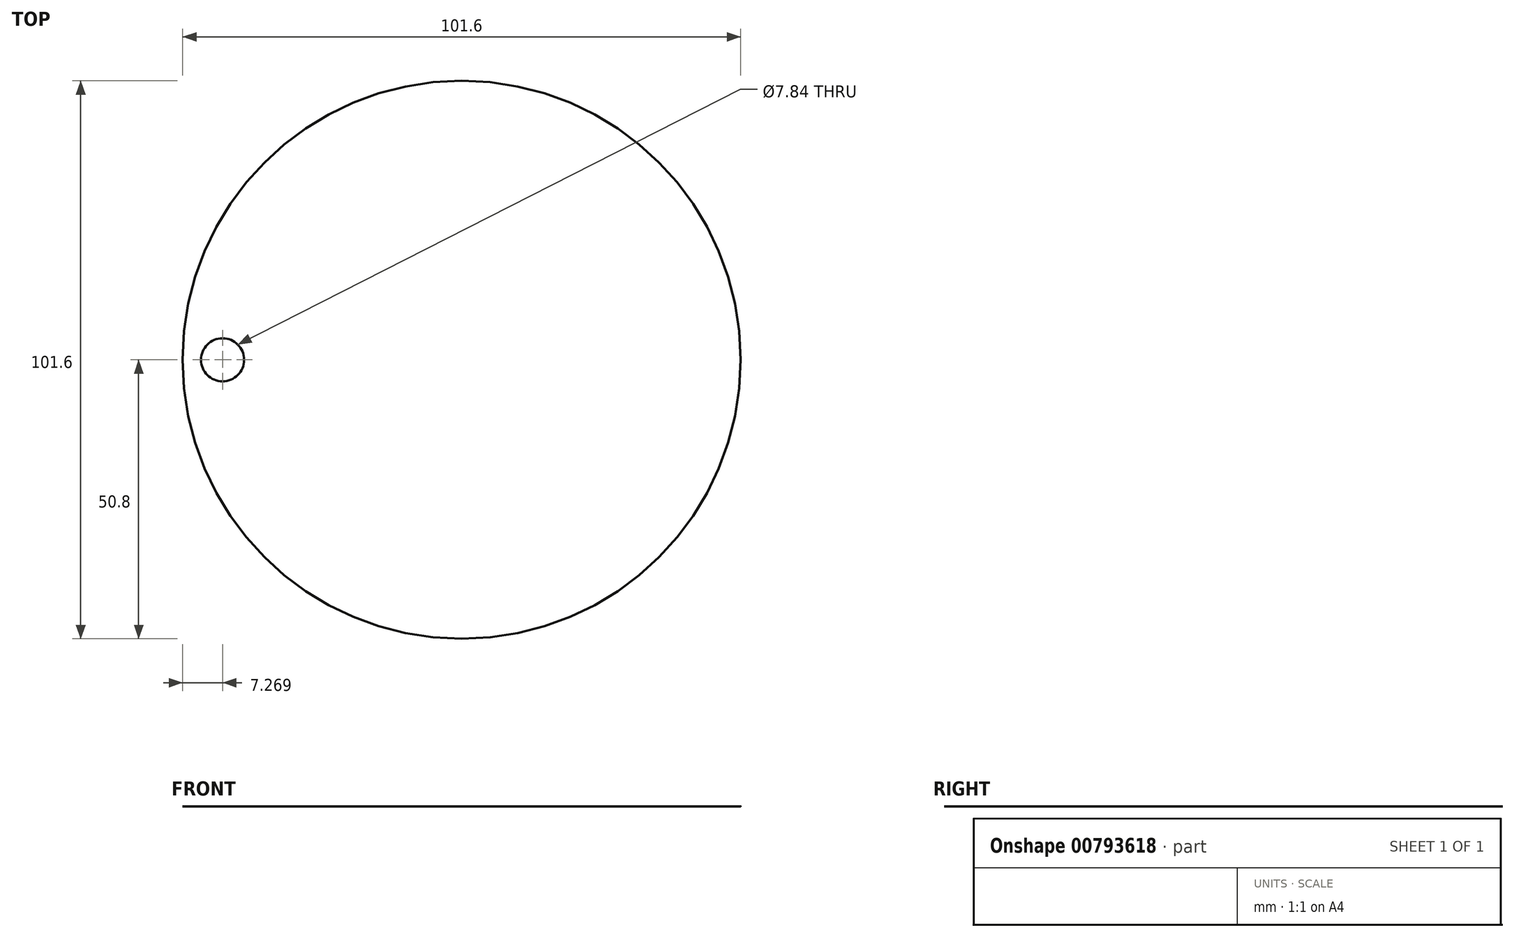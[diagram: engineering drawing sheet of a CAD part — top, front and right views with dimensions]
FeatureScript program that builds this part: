
annotation { "Feature Type Name" : "Feature", "Feature Type Description" : "" }
export const myFeature = defineFeature(function(context is Context, id is Id, definition is map)
    precondition{}
    {
        {
            var Q0;
            Q0=qCreatedBy(makeId("Top.planeOp"),FACE);
            var sketch = newSketch(context, id + "F0", { "sketchPlane" : qUnion([Q0])});
            skCircle(sketch, "E0", {"center": v(0, 0) * mm, "radius": 50.8 * mm});
            skSolve(sketch);
        }
        {
            var Q0;
            Q0=makeQuery(id+"F0.imprint","IMPRINT",FACE,{"disambiguationData":[TD([[makeQuery(id+"F0.imprint","IMPRINT",EDGE,{"derivedFrom":sQuery(id+"F0.wireOp",EDGE,"E0")}),1.0]])]});
            extrude(context, id + "F1", {"entities" : qUnion([Q0]), "depth" : 1 / 203.2 * mm, "offsetDistance" : 25.4 * mm});
        }
        {
            var Q0;
            Q0=makeQuery(id+"F1.opExtrude","CAP_FACE",FACE,{"disambiguationData":[OSD([sQuery(id+"F0.wireOp",EDGE,"E0")])],"isStart":false});
            var sketch = newSketch(context, id + "F2", { "sketchPlane" : qUnion([Q0])});
            skCircle(sketch, "E1", {"center": v(-43.53, 0) * mm, "radius": 3.92 * mm});
            skSolve(sketch);
        }
        {
            var Q0;
            Q0=makeQuery(id+"F2.imprint","IMPRINT",FACE,{"disambiguationData":[TD([[makeQuery(id+"F2.imprint","IMPRINT",EDGE,{"derivedFrom":sQuery(id+"F2.wireOp",EDGE,"E1")}),1.0]])]});
            extrude(context, id + "F3", {"entities" : qUnion([Q0]), "operationType" : NewBodyOperationType.REMOVE, "oppositeDirection" : true, "depth" : 25.4 * mm, "offsetDistance" : 25.4 * mm});
        }
    });
